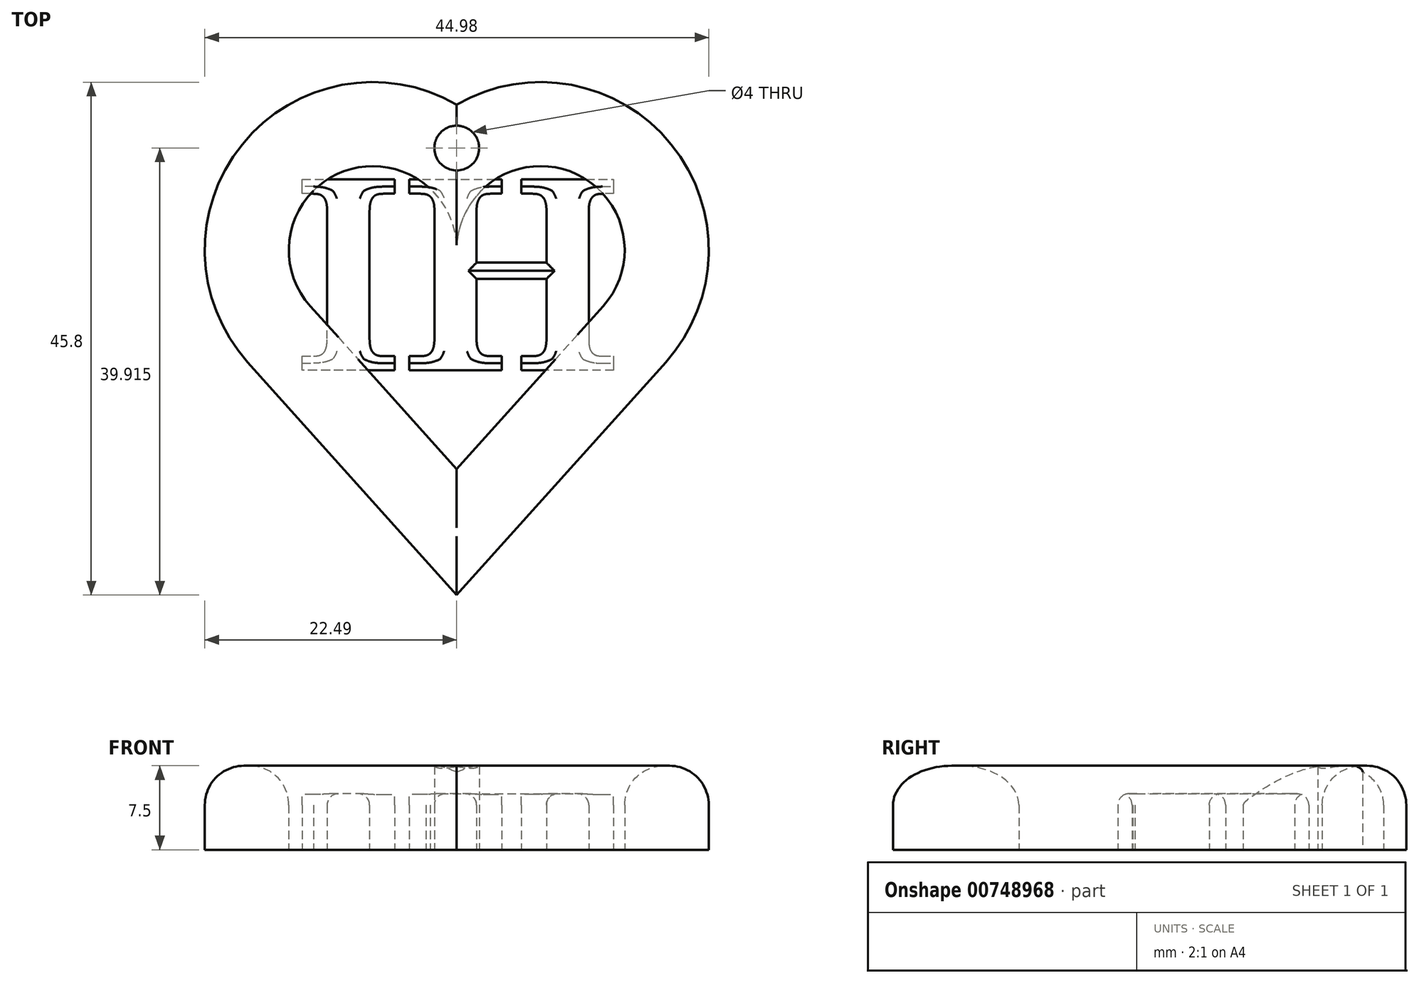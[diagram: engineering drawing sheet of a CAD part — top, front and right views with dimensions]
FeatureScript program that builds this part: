
annotation { "Feature Type Name" : "Feature", "Feature Type Description" : "" }
export const myFeature = defineFeature(function(context is Context, id is Id, definition is map)
    precondition{}
    {
        {
            var Q0;
            Q0=qCreatedBy(makeId("Top.planeOp"),FACE);
            var sketch = newSketch(context, id + "F0", { "sketchPlane" : qUnion([Q0])});
            skLineSegment(sketch, "E0", {"start": v(0, 31.52) * mm, "end": v(0, -50.1) * mm, "construction": true});
            skLineSegment(sketch, "E1", {"start": v(-13.07, 26.08) * mm, "end": v(0, 31.52) * mm, "construction": true});
            skArc(sketch, "E2", {"start": v(0, 31.52) * mm, "mid": v(-10.37, 38.02) * mm, "end": v(-13.07, 26.08) * mm});
            skLineSegment(sketch, "E3", {"start": v(-13.07, 26.08) * mm, "end": v(0, 11.52) * mm});
            skPoint(sketch, "E4.orphan", {"position": v(0, 31.52) * mm});
            skLineSegment(sketch, "E5.MirrorCS", {"start": v(13.07, 26.08) * mm, "end": v(0, 31.52) * mm, "construction": true});
            skArc(sketch, "E6.MirrorCS", {"start": v(0, 31.52) * mm, "mid": v(10.37, 38.02) * mm, "end": v(13.07, 26.08) * mm});
            skLineSegment(sketch, "E7.MirrorCS", {"start": v(13.07, 26.08) * mm, "end": v(0, 11.52) * mm});
            skLineSegment(sketch, "E8.0", {"start": v(-18.65, 21.07) * mm, "end": v(0, 0.3) * mm});
            skArc(sketch, "E8.1", {"start": v(0, 44.09) * mm, "mid": v(-19.14, 40.53) * mm, "end": v(-18.65, 21.07) * mm});
            skArc(sketch, "E8.2", {"start": v(0, 44.09) * mm, "mid": v(19.14, 40.53) * mm, "end": v(18.65, 21.07) * mm});
            skLineSegment(sketch, "E8.3", {"start": v(18.65, 21.07) * mm, "end": v(0, 0.3) * mm});
            skCircle(sketch, "E9", {"center": v(0, 40.2) * mm, "radius": 2 * mm});
            skSolve(sketch);
        }
        {
            var Q0;
            Q0=qCreatedBy(makeId("Top.planeOp"),FACE);
            var sketch = newSketch(context, id + "F1", { "sketchPlane" : qUnion([Q0])});
            skPoint(sketch, "E10.0", {"position": v(0, 31.52) * mm});
            skText(sketch, "E11", { "text": "IH", "fontName": "NotoSerif-Bold.ttf"});
            const initialGuessF1  = {"E11": [-0.01446, 0.02035, 1, 0, 0.01719]};
            skSetInitialGuess(sketch, initialGuessF1);
            skSolve(sketch);
        }
        {
            var Q0;
            Q0=makeQuery(id+"F0.imprint","IMPRINT",FACE,{"disambiguationData":[TD([[makeQuery(id+"F0.imprint","IMPRINT",EDGE,{"derivedFrom":sQuery(id+"F0.wireOp",EDGE,"E2")}),-1.0]])]});
            extrude(context, id + "F2", {"entities" : qUnion([Q0]), "depth" : 7.5 * mm, "offsetDistance" : 25 * mm});
        }
        {
            var Q0;
            Q0=makeQuery(id+"F2.opExtrude","CAP_EDGE",EDGE,{"disambiguationData":[OSD([sQuery(id+"F0.wireOp",EDGE,"E6.MirrorCS")])],"isStart":false});
            var Q1;
            Q1=makeQuery(id+"F2.opExtrude","CAP_EDGE",EDGE,{"disambiguationData":[OSD([sQuery(id+"F0.wireOp",EDGE,"E2")])],"isStart":false});
            var Q2;
            Q2=makeQuery(id+"F2.opExtrude","CAP_EDGE",EDGE,{"disambiguationData":[OSD([sQuery(id+"F0.wireOp",EDGE,"E8.1")])],"isStart":false});
            var Q3;
            Q3=makeQuery(id+"F2.opExtrude","CAP_EDGE",EDGE,{"disambiguationData":[OSD([sQuery(id+"F0.wireOp",EDGE,"E3")])],"isStart":false});
            var Q4;
            Q4=makeQuery(id+"F2.opExtrude","CAP_EDGE",EDGE,{"disambiguationData":[OSD([sQuery(id+"F0.wireOp",EDGE,"E8.2")])],"isStart":false});
            fillet(context, id + "F3", {"entities" : qUnion([Q0, Q1, Q2, Q3, Q4]), "radius" : 3.5 * mm, "tangentPropagation" : true, "allowEdgeOverflow" : false});
        }
        {
            var Q0;
            Q0=makeQuery(id+"F1.imprint","IMPRINT",FACE,{"disambiguationData":[TD([[makeQuery(id+"F1.imprint","IMPRINT",EDGE,{"derivedFrom":sQuery(id+"F1.wireOp",EDGE,"E11.sketch_text.stroke-0")}),-1.0]])]});
            var Q1;
            Q1=makeQuery(id+"F1.imprint","IMPRINT",FACE,{"disambiguationData":[TD([[makeQuery(id+"F1.imprint","IMPRINT",EDGE,{"derivedFrom":sQuery(id+"F1.wireOp",EDGE,"E11.sketch_text.stroke-28")}),-1.0]])]});
            extrude(context, id + "F4", {"entities" : qUnion([Q0, Q1]), "depth" : 5 * mm, "offsetDistance" : 25 * mm});
        }
        {
            var Q0;
            Q0=makeQuery(id+"F4.opExtrude","CAP_FACE",FACE,{"disambiguationData":[OSD([sQuery(id+"F1.wireOp",EDGE,"E11.sketch_text.stroke-28"),sQuery(id+"F1.wireOp",EDGE,"E11.sketch_text.stroke-29"),sQuery(id+"F1.wireOp",EDGE,"E11.sketch_text.stroke-30"),sQuery(id+"F1.wireOp",EDGE,"E11.sketch_text.stroke-31"),sQuery(id+"F1.wireOp",EDGE,"E11.sketch_text.stroke-32"),sQuery(id+"F1.wireOp",EDGE,"E11.sketch_text.stroke-33"),sQuery(id+"F1.wireOp",EDGE,"E11.sketch_text.stroke-34"),sQuery(id+"F1.wireOp",EDGE,"E11.sketch_text.stroke-35"),sQuery(id+"F1.wireOp",EDGE,"E11.sketch_text.stroke-36"),sQuery(id+"F1.wireOp",EDGE,"E11.sketch_text.stroke-37"),sQuery(id+"F1.wireOp",EDGE,"E11.sketch_text.stroke-38"),sQuery(id+"F1.wireOp",EDGE,"E11.sketch_text.stroke-39"),sQuery(id+"F1.wireOp",EDGE,"E11.sketch_text.stroke-40"),sQuery(id+"F1.wireOp",EDGE,"E11.sketch_text.stroke-41"),sQuery(id+"F1.wireOp",EDGE,"E11.sketch_text.stroke-42"),sQuery(id+"F1.wireOp",EDGE,"E11.sketch_text.stroke-43"),sQuery(id+"F1.wireOp",EDGE,"E11.sketch_text.stroke-44"),sQuery(id+"F1.wireOp",EDGE,"E11.sketch_text.stroke-45"),sQuery(id+"F1.wireOp",EDGE,"E11.sketch_text.stroke-46"),sQuery(id+"F1.wireOp",EDGE,"E11.sketch_text.stroke-47"),sQuery(id+"F1.wireOp",EDGE,"E11.sketch_text.stroke-48"),sQuery(id+"F1.wireOp",EDGE,"E11.sketch_text.stroke-49"),sQuery(id+"F1.wireOp",EDGE,"E11.sketch_text.stroke-50"),sQuery(id+"F1.wireOp",EDGE,"E11.sketch_text.stroke-51"),sQuery(id+"F1.wireOp",EDGE,"E11.sketch_text.stroke-52"),sQuery(id+"F1.wireOp",EDGE,"E11.sketch_text.stroke-53"),sQuery(id+"F1.wireOp",EDGE,"E11.sketch_text.stroke-54"),sQuery(id+"F1.wireOp",EDGE,"E11.sketch_text.stroke-55"),sQuery(id+"F1.wireOp",EDGE,"E11.sketch_text.stroke-56"),sQuery(id+"F1.wireOp",EDGE,"E11.sketch_text.stroke-57"),sQuery(id+"F1.wireOp",EDGE,"E11.sketch_text.stroke-58"),sQuery(id+"F1.wireOp",EDGE,"E11.sketch_text.stroke-59"),sQuery(id+"F1.wireOp",EDGE,"E11.sketch_text.stroke-60"),sQuery(id+"F1.wireOp",EDGE,"E11.sketch_text.stroke-61"),sQuery(id+"F1.wireOp",EDGE,"E11.sketch_text.stroke-62"),sQuery(id+"F1.wireOp",EDGE,"E11.sketch_text.stroke-63"),sQuery(id+"F1.wireOp",EDGE,"E11.sketch_text.stroke-64"),sQuery(id+"F1.wireOp",EDGE,"E11.sketch_text.stroke-65"),sQuery(id+"F1.wireOp",EDGE,"E11.sketch_text.stroke-66"),sQuery(id+"F1.wireOp",EDGE,"E11.sketch_text.stroke-67"),sQuery(id+"F1.wireOp",EDGE,"E11.sketch_text.stroke-68"),sQuery(id+"F1.wireOp",EDGE,"E11.sketch_text.stroke-69"),sQuery(id+"F1.wireOp",EDGE,"E11.sketch_text.stroke-70"),sQuery(id+"F1.wireOp",EDGE,"E11.sketch_text.stroke-71"),sQuery(id+"F1.wireOp",EDGE,"E11.sketch_text.stroke-72"),sQuery(id+"F1.wireOp",EDGE,"E11.sketch_text.stroke-73"),sQuery(id+"F1.wireOp",EDGE,"E11.sketch_text.stroke-74"),sQuery(id+"F1.wireOp",EDGE,"E11.sketch_text.stroke-75"),sQuery(id+"F1.wireOp",EDGE,"E11.sketch_text.stroke-76"),sQuery(id+"F1.wireOp",EDGE,"E11.sketch_text.stroke-77"),sQuery(id+"F1.wireOp",EDGE,"E11.sketch_text.stroke-78"),sQuery(id+"F1.wireOp",EDGE,"E11.sketch_text.stroke-79"),sQuery(id+"F1.wireOp",EDGE,"E11.sketch_text.stroke-80"),sQuery(id+"F1.wireOp",EDGE,"E11.sketch_text.stroke-81"),sQuery(id+"F1.wireOp",EDGE,"E11.sketch_text.stroke-82"),sQuery(id+"F1.wireOp",EDGE,"E11.sketch_text.stroke-83"),sQuery(id+"F1.wireOp",EDGE,"E11.sketch_text.stroke-84"),sQuery(id+"F1.wireOp",EDGE,"E11.sketch_text.stroke-85"),sQuery(id+"F1.wireOp",EDGE,"E11.sketch_text.stroke-86"),sQuery(id+"F1.wireOp",EDGE,"E11.sketch_text.stroke-87")])],"isStart":false});
            var Q1;
            Q1=makeQuery(id+"F4.opExtrude","CAP_FACE",FACE,{"disambiguationData":[OSD([sQuery(id+"F1.wireOp",EDGE,"E11.sketch_text.stroke-0"),sQuery(id+"F1.wireOp",EDGE,"E11.sketch_text.stroke-1"),sQuery(id+"F1.wireOp",EDGE,"E11.sketch_text.stroke-2"),sQuery(id+"F1.wireOp",EDGE,"E11.sketch_text.stroke-3"),sQuery(id+"F1.wireOp",EDGE,"E11.sketch_text.stroke-4"),sQuery(id+"F1.wireOp",EDGE,"E11.sketch_text.stroke-5"),sQuery(id+"F1.wireOp",EDGE,"E11.sketch_text.stroke-6"),sQuery(id+"F1.wireOp",EDGE,"E11.sketch_text.stroke-7"),sQuery(id+"F1.wireOp",EDGE,"E11.sketch_text.stroke-8"),sQuery(id+"F1.wireOp",EDGE,"E11.sketch_text.stroke-9"),sQuery(id+"F1.wireOp",EDGE,"E11.sketch_text.stroke-10"),sQuery(id+"F1.wireOp",EDGE,"E11.sketch_text.stroke-11"),sQuery(id+"F1.wireOp",EDGE,"E11.sketch_text.stroke-12"),sQuery(id+"F1.wireOp",EDGE,"E11.sketch_text.stroke-13"),sQuery(id+"F1.wireOp",EDGE,"E11.sketch_text.stroke-14"),sQuery(id+"F1.wireOp",EDGE,"E11.sketch_text.stroke-15"),sQuery(id+"F1.wireOp",EDGE,"E11.sketch_text.stroke-16"),sQuery(id+"F1.wireOp",EDGE,"E11.sketch_text.stroke-17"),sQuery(id+"F1.wireOp",EDGE,"E11.sketch_text.stroke-18"),sQuery(id+"F1.wireOp",EDGE,"E11.sketch_text.stroke-19"),sQuery(id+"F1.wireOp",EDGE,"E11.sketch_text.stroke-20"),sQuery(id+"F1.wireOp",EDGE,"E11.sketch_text.stroke-21"),sQuery(id+"F1.wireOp",EDGE,"E11.sketch_text.stroke-22"),sQuery(id+"F1.wireOp",EDGE,"E11.sketch_text.stroke-23"),sQuery(id+"F1.wireOp",EDGE,"E11.sketch_text.stroke-24"),sQuery(id+"F1.wireOp",EDGE,"E11.sketch_text.stroke-25"),sQuery(id+"F1.wireOp",EDGE,"E11.sketch_text.stroke-26"),sQuery(id+"F1.wireOp",EDGE,"E11.sketch_text.stroke-27")])],"isStart":false});
            fillet(context, id + "F5", {"entities" : qUnion([Q0, Q1]), "radius" : 1 * mm, "tangentPropagation" : true, "allowEdgeOverflow" : false});
        }
    });
